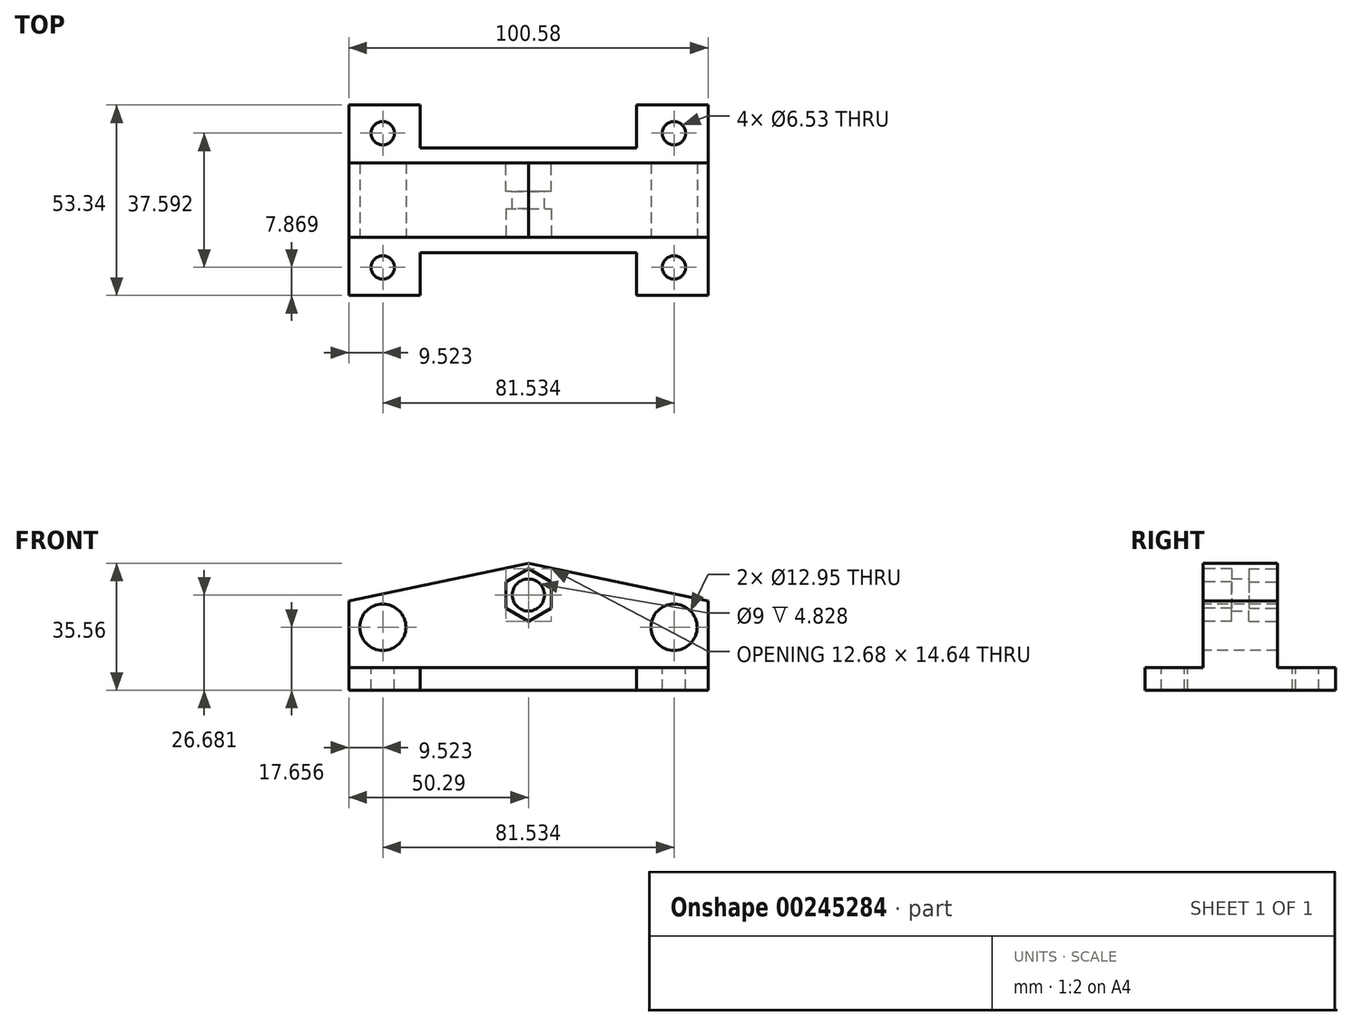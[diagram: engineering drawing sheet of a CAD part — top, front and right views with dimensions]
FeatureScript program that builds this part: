
annotation { "Feature Type Name" : "Feature", "Feature Type Description" : "" }
export const myFeature = defineFeature(function(context is Context, id is Id, definition is map)
    precondition{}
    {
        {
            var Q0;
            Q0=qCreatedBy(makeId("Top.planeOp"),FACE);
            var sketch = newSketch(context, id + "F0", { "sketchPlane" : qUnion([Q0])});
            skLineSegment(sketch, "E0.bottom", {"start": v(-48.14, 27.76) * mm, "end": v(52.44, 27.76) * mm});
            skLineSegment(sketch, "E0.top", {"start": v(-48.14, -25.58) * mm, "end": v(52.44, -25.58) * mm});
            skLineSegment(sketch, "E0.left", {"start": v(-48.14, 27.76) * mm, "end": v(-48.14, -25.58) * mm});
            skLineSegment(sketch, "E0.right", {"start": v(52.44, 27.76) * mm, "end": v(52.44, -25.58) * mm});
            skSolve(sketch);
        }
        {
            var Q0;
            Q0=qSketchRegion(id+"F0",true);
            extrude(context, id + "F1", {"entities" : qUnion([Q0]), "depth" : 6.35 * mm});
        }
        {
            var Q0;
            Q0=makeQuery(id+"F1.opExtrude","CAP_FACE",FACE,{"disambiguationData":[OSD([sQuery(id+"F0.wireOp",EDGE,"E0.bottom"),sQuery(id+"F0.wireOp",EDGE,"E0.top"),sQuery(id+"F0.wireOp",EDGE,"E0.left"),sQuery(id+"F0.wireOp",EDGE,"E0.right")])],"isStart":false});
            var sketch = newSketch(context, id + "F2", { "sketchPlane" : qUnion([Q0])});
            skLineSegment(sketch, "E1.bottom", {"start": v(-48.14, 11.5) * mm, "end": v(52.44, 11.5) * mm});
            skLineSegment(sketch, "E1.top", {"start": v(-48.14, -9.33) * mm, "end": v(52.44, -9.33) * mm});
            skLineSegment(sketch, "E1.left", {"start": v(-48.14, 11.5) * mm, "end": v(-48.14, -9.33) * mm});
            skLineSegment(sketch, "E1.right", {"start": v(52.44, 11.5) * mm, "end": v(52.44, -9.33) * mm});
            skSolve(sketch);
        }
        {
            var Q0;
            Q0=qSketchRegion(id+"F2",true);
            extrude(context, id + "F3", {"entities" : qUnion([Q0]), "operationType" : NewBodyOperationType.ADD, "depth" : 29.21 * mm});
        }
        {
            var Q0;
            Q0=makeQuery(id+"F3.opExtrude","SWEPT_FACE",FACE,{"disambiguationData":[OSD([sQuery(id+"F2.wireOp",EDGE,"E1.top")])]});
            var sketch = newSketch(context, id + "F4", { "sketchPlane" : qUnion([Q0])});
            skCircle(sketch, "E2.cCircle", {"center": v(2.15, 26.68) * mm, "radius": 6.34 * mm, "construction": true});
            skLineSegment(sketch, "E2.0", {"start": v(8.49, 30.34) * mm, "end": v(8.49, 23.02) * mm});
            skLineSegment(sketch, "E2.1", {"start": v(8.49, 23.02) * mm, "end": v(2.15, 19.36) * mm});
            skLineSegment(sketch, "E2.2", {"start": v(2.15, 19.36) * mm, "end": v(-4.2, 23.02) * mm});
            skLineSegment(sketch, "E2.3", {"start": v(-4.2, 23.02) * mm, "end": v(-4.2, 30.34) * mm});
            skLineSegment(sketch, "E2.4", {"start": v(-4.2, 30.34) * mm, "end": v(2.15, 34) * mm});
            skLineSegment(sketch, "E2.5", {"start": v(2.15, 34) * mm, "end": v(8.49, 30.34) * mm});
            skPoint(sketch, "E2.0.midPoint", {"position": v(8.49, 26.68) * mm});
            skSolve(sketch);
        }
        {
            var Q0;
            Q0=qSketchRegion(id+"F4",true);
            extrude(context, id + "F5", {"entities" : qUnion([Q0]), "operationType" : NewBodyOperationType.REMOVE, "oppositeDirection" : true, "depth" : 8 * mm});
        }
        {
            var Q0;
            Q0=makeQuery(id+"F3.opExtrude","SWEPT_FACE",FACE,{"disambiguationData":[OSD([sQuery(id+"F2.wireOp",EDGE,"E1.bottom")])]});
            var sketch = newSketch(context, id + "F6", { "sketchPlane" : qUnion([Q0])});
            skCircle(sketch, "E3.cCircle", {"center": v(-2.15, 26.68) * mm, "radius": 6.34 * mm, "construction": true});
            skLineSegment(sketch, "E3.0", {"start": v(4.2, 30.34) * mm, "end": v(4.2, 23.02) * mm});
            skLineSegment(sketch, "E3.1", {"start": v(4.2, 23.02) * mm, "end": v(-2.15, 19.36) * mm});
            skLineSegment(sketch, "E3.2", {"start": v(-2.15, 19.36) * mm, "end": v(-8.49, 23.02) * mm});
            skLineSegment(sketch, "E3.3", {"start": v(-8.49, 23.02) * mm, "end": v(-8.49, 30.34) * mm});
            skLineSegment(sketch, "E3.4", {"start": v(-8.49, 30.34) * mm, "end": v(-2.15, 34) * mm});
            skLineSegment(sketch, "E3.5", {"start": v(-2.15, 34) * mm, "end": v(4.2, 30.34) * mm});
            skPoint(sketch, "E3.0.midPoint", {"position": v(4.2, 26.68) * mm});
            skSolve(sketch);
        }
        {
            var Q0;
            Q0=qSketchRegion(id+"F6",true);
            extrude(context, id + "F7", {"entities" : qUnion([Q0]), "operationType" : NewBodyOperationType.REMOVE, "oppositeDirection" : true, "depth" : 8 * mm});
        }
        {
            var Q0;
            Q0=makeQuery(id+"F3.opExtrude","SWEPT_FACE",FACE,{"disambiguationData":[OSD([sQuery(id+"F2.wireOp",EDGE,"E1.bottom")])]});
            var sketch = newSketch(context, id + "F8", { "sketchPlane" : qUnion([Q0])});
            skPoint(sketch, "E4", {"position": v(-2.15, 26.68) * mm});
            skPoint(sketch, "E4.positionSnap0", {"position": v(4.2, 26.68) * mm});
            skSolve(sketch);
        }
        {
            var Q0;
            Q0=sQuery(id+"F8.wireOp",VERTEX,"E4");
            var Q1;
            Q1=makeQuery(id+"F1.opExtrude","SWEPT_BODY",BODY,{"disambiguationData":[OSD([sQuery(id+"F0.wireOp",EDGE,"E0.bottom"),sQuery(id+"F0.wireOp",EDGE,"E0.top"),sQuery(id+"F0.wireOp",EDGE,"E0.left"),sQuery(id+"F0.wireOp",EDGE,"E0.right")])]});
            hole(context, id + "F9", {"style" : HoleStyle.SIMPLE, "endStyle" : HoleEndStyle.THROUGH, "holeDiameter" : 9 * mm, "tappedDepth" : 12 * mm, "tapClearance" : 3, "locations" : qUnion([Q0]), "scope" : qUnion([Q1])});
        }
        {
            var Q0;
            Q0=makeQuery(id+"F3.opExtrude","SWEPT_FACE",FACE,{"disambiguationData":[OSD([sQuery(id+"F2.wireOp",EDGE,"E1.top")])]});
            var sketch = newSketch(context, id + "F10", { "sketchPlane" : qUnion([Q0])});
            skPoint(sketch, "E5", {"position": v(-38.62, 17.66) * mm});
            skPoint(sketch, "E6", {"position": v(42.92, 17.66) * mm});
            skSolve(sketch);
        }
        {
            var Q0;
            Q0=sQuery(id+"F10.wireOp",VERTEX,"E6");
            var Q1;
            Q1=sQuery(id+"F10.wireOp",VERTEX,"E5");
            var Q2;
            Q2=makeQuery(id+"F1.opExtrude","SWEPT_BODY",BODY,{"disambiguationData":[OSD([sQuery(id+"F0.wireOp",EDGE,"E0.bottom"),sQuery(id+"F0.wireOp",EDGE,"E0.top"),sQuery(id+"F0.wireOp",EDGE,"E0.left"),sQuery(id+"F0.wireOp",EDGE,"E0.right")])]});
            hole(context, id + "F11", {"style" : HoleStyle.SIMPLE, "endStyle" : HoleEndStyle.THROUGH, "holeDiameter" : 12.95 * mm, "tappedDepth" : 12 * mm, "tapClearance" : 3, "locations" : qUnion([Q0, Q1]), "scope" : qUnion([Q2])});
        }
        {
            var Q0;
            {var subQ0=sQuery(id+"F0.wireOp",EDGE,"E0.right");var subQ1=sQuery(id+"F0.wireOp",EDGE,"E0.left");var subQ2=sQuery(id+"F0.wireOp",EDGE,"E0.top");Q0=makeQuery(id+"F3.boolean.opBoolean","SPLIT",FACE,{"disambiguationData":[TD([makeQuery(id+"F1.opExtrude","SWEPT_FACE",FACE,{"disambiguationData":[OSD([subQ2])]})])],"derivedFrom":makeQuery(id+"F1.opExtrude","CAP_FACE",FACE,{"disambiguationData":[OSD([sQuery(id+"F0.wireOp",EDGE,"E0.bottom"),subQ2,subQ1,subQ0])],"isStart":false})});}
            var sketch = newSketch(context, id + "F12", { "sketchPlane" : qUnion([Q0])});
            skPoint(sketch, "E7", {"position": v(-38.62, -17.71) * mm});
            skPoint(sketch, "E8", {"position": v(42.92, -17.71) * mm});
            skPoint(sketch, "E9", {"position": v(42.92, 19.88) * mm});
            skPoint(sketch, "E10", {"position": v(-38.62, 19.88) * mm});
            skSolve(sketch);
        }
        {
            var Q0;
            Q0=sQuery(id+"F12.wireOp",VERTEX,"E7");
            var Q1;
            Q1=sQuery(id+"F12.wireOp",VERTEX,"E10");
            var Q2;
            Q2=sQuery(id+"F12.wireOp",VERTEX,"E9");
            var Q3;
            Q3=sQuery(id+"F12.wireOp",VERTEX,"E8");
            var Q4;
            Q4=makeQuery(id+"F1.opExtrude","SWEPT_BODY",BODY,{"disambiguationData":[OSD([sQuery(id+"F0.wireOp",EDGE,"E0.bottom"),sQuery(id+"F0.wireOp",EDGE,"E0.top"),sQuery(id+"F0.wireOp",EDGE,"E0.left"),sQuery(id+"F0.wireOp",EDGE,"E0.right")])]});
            hole(context, id + "F13", {"style" : HoleStyle.SIMPLE, "endStyle" : HoleEndStyle.THROUGH, "holeDiameter" : 6.53 * mm, "tappedDepth" : 12 * mm, "tapClearance" : 3, "locations" : qUnion([Q0, Q1, Q2, Q3]), "scope" : qUnion([Q4])});
        }
        {
            var Q0;
            {var subQ0=sQuery(id+"F0.wireOp",EDGE,"E0.right");var subQ1=sQuery(id+"F0.wireOp",EDGE,"E0.left");var subQ2=sQuery(id+"F0.wireOp",EDGE,"E0.bottom");Q0=makeQuery(id+"F3.boolean.opBoolean","SPLIT",FACE,{"disambiguationData":[TD([makeQuery(id+"F1.opExtrude","SWEPT_FACE",FACE,{"disambiguationData":[OSD([subQ2])]})])],"derivedFrom":makeQuery(id+"F1.opExtrude","CAP_FACE",FACE,{"disambiguationData":[OSD([subQ2,sQuery(id+"F0.wireOp",EDGE,"E0.top"),subQ1,subQ0])],"isStart":false})});}
            var sketch = newSketch(context, id + "F14", { "sketchPlane" : qUnion([Q0])});
            skLineSegment(sketch, "E11.bottom", {"start": v(-28.14, 27.76) * mm, "end": v(32.44, 27.76) * mm});
            skLineSegment(sketch, "E11.top", {"start": v(-28.14, 15.76) * mm, "end": v(32.44, 15.76) * mm});
            skLineSegment(sketch, "E11.left", {"start": v(-28.14, 27.76) * mm, "end": v(-28.14, 15.76) * mm});
            skLineSegment(sketch, "E11.right", {"start": v(32.44, 27.76) * mm, "end": v(32.44, 15.76) * mm});
            skSolve(sketch);
        }
        {
            var Q0;
            Q0=makeQuery(id+"F14.imprint","IMPRINT",FACE,{"disambiguationData":[TD([[makeQuery(id+"F14.imprint","IMPRINT",EDGE,{"derivedFrom":sQuery(id+"F14.wireOp",EDGE,"E11.bottom")}),-1.0]])]});
            extrude(context, id + "F15", {"entities" : qUnion([Q0]), "operationType" : NewBodyOperationType.REMOVE, "endBound" : BoundingType.UP_TO_NEXT, "oppositeDirection" : true, "depth" : 25 * mm});
        }
        {
            var Q0;
            {var subQ0=sQuery(id+"F0.wireOp",EDGE,"E0.right");var subQ1=sQuery(id+"F0.wireOp",EDGE,"E0.left");var subQ2=sQuery(id+"F0.wireOp",EDGE,"E0.top");Q0=makeQuery(id+"F3.boolean.opBoolean","SPLIT",FACE,{"disambiguationData":[TD([makeQuery(id+"F1.opExtrude","SWEPT_FACE",FACE,{"disambiguationData":[OSD([subQ2])]})])],"derivedFrom":makeQuery(id+"F1.opExtrude","CAP_FACE",FACE,{"disambiguationData":[OSD([sQuery(id+"F0.wireOp",EDGE,"E0.bottom"),subQ2,subQ1,subQ0])],"isStart":false})});}
            var sketch = newSketch(context, id + "F16", { "sketchPlane" : qUnion([Q0])});
            skLineSegment(sketch, "E12.bottom", {"start": v(-28.14, -25.58) * mm, "end": v(32.44, -25.58) * mm});
            skLineSegment(sketch, "E12.top", {"start": v(-28.14, -13.58) * mm, "end": v(32.44, -13.58) * mm});
            skLineSegment(sketch, "E12.left", {"start": v(-28.14, -25.58) * mm, "end": v(-28.14, -13.58) * mm});
            skLineSegment(sketch, "E12.right", {"start": v(32.44, -25.58) * mm, "end": v(32.44, -13.58) * mm});
            skSolve(sketch);
        }
        {
            var Q0;
            Q0=qSketchRegion(id+"F16",true);
            extrude(context, id + "F17", {"entities" : qUnion([Q0]), "operationType" : NewBodyOperationType.REMOVE, "endBound" : BoundingType.UP_TO_NEXT, "oppositeDirection" : true, "depth" : 25 * mm});
        }
        {
            var Q0;
            Q0=makeQuery(id+"F3.opExtrude","SWEPT_FACE",FACE,{"disambiguationData":[OSD([sQuery(id+"F2.wireOp",EDGE,"E1.top")])]});
            var sketch = newSketch(context, id + "F18", { "sketchPlane" : qUnion([Q0])});
            skLineSegment(sketch, "E13", {"start": v(2.15, 35.56) * mm, "end": v(52.44, 25.01) * mm});
            skLineSegment(sketch, "E14", {"start": v(52.44, 25.01) * mm, "end": v(52.44, 35.56) * mm});
            skLineSegment(sketch, "E15", {"start": v(52.44, 35.56) * mm, "end": v(2.15, 35.56) * mm});
            skLineSegment(sketch, "E16", {"start": v(2.15, 35.56) * mm, "end": v(-48.14, 25.01) * mm});
            skLineSegment(sketch, "E17", {"start": v(-48.14, 25.01) * mm, "end": v(-48.14, 35.56) * mm});
            skLineSegment(sketch, "E18", {"start": v(-48.14, 35.56) * mm, "end": v(2.15, 35.56) * mm});
            skSolve(sketch);
        }
        {
            var Q0;
            Q0=makeQuery(id+"F18.imprint","IMPRINT",FACE,{"disambiguationData":[TD([[makeQuery(id+"F18.imprint","IMPRINT",EDGE,{"derivedFrom":sQuery(id+"F18.wireOp",EDGE,"E16")}),-1.0]])]});
            var Q1;
            Q1=makeQuery(id+"F18.imprint","IMPRINT",FACE,{"disambiguationData":[TD([[makeQuery(id+"F18.imprint","IMPRINT",EDGE,{"derivedFrom":sQuery(id+"F18.wireOp",EDGE,"E13")}),1.0]])]});
            extrude(context, id + "F19", {"entities" : qUnion([Q0, Q1]), "operationType" : NewBodyOperationType.REMOVE, "endBound" : BoundingType.UP_TO_NEXT, "oppositeDirection" : true, "depth" : 25 * mm});
        }
    });
